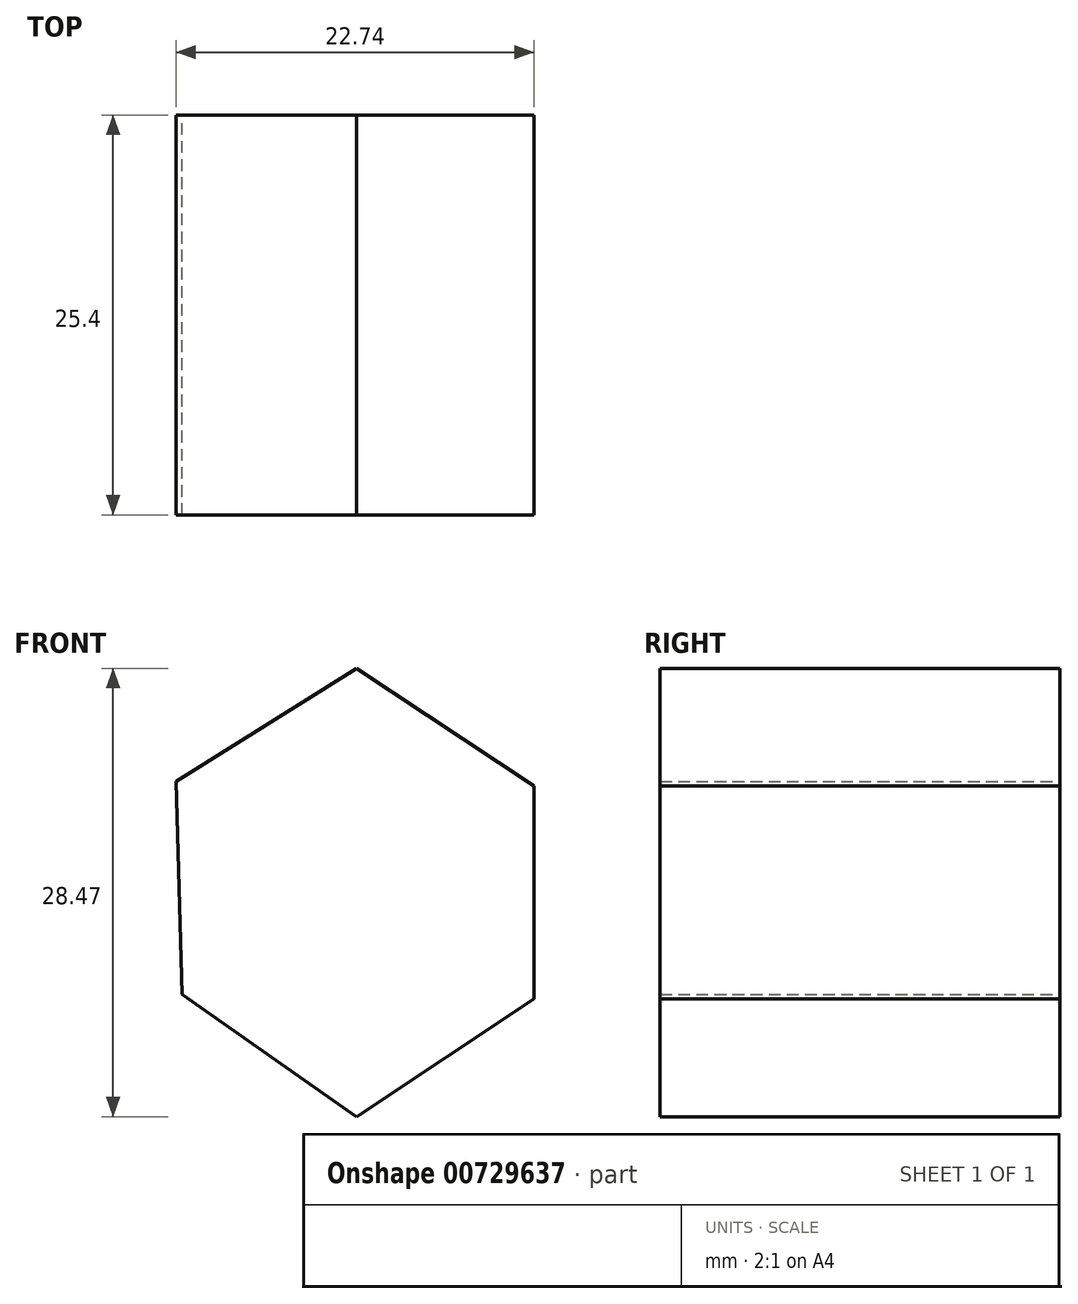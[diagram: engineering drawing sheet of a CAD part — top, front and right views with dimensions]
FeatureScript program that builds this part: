
annotation { "Feature Type Name" : "Feature", "Feature Type Description" : "" }
export const myFeature = defineFeature(function(context is Context, id is Id, definition is map)
    precondition{}
    {
        {
            var Q0;
            Q0=qCreatedBy(makeId("Front.planeOp"),FACE);
            var sketch = newSketch(context, id + "F0", { "sketchPlane" : qUnion([Q0])});
            skLineSegment(sketch, "E0", {"start": v(-53.1, 41.59) * mm, "end": v(-41.64, 48.77) * mm});
            skLineSegment(sketch, "E1", {"start": v(-41.64, 48.77) * mm, "end": v(-30.36, 41.3) * mm});
            skLineSegment(sketch, "E2", {"start": v(-30.36, 41.3) * mm, "end": v(-30.36, 27.77) * mm});
            skLineSegment(sketch, "E3", {"start": v(-30.36, 27.77) * mm, "end": v(-41.64, 20.3) * mm});
            skLineSegment(sketch, "E4", {"start": v(-41.64, 20.3) * mm, "end": v(-52.71, 28.07) * mm});
            skLineSegment(sketch, "E5", {"start": v(-52.71, 28.07) * mm, "end": v(-53.1, 41.59) * mm});
            skSolve(sketch);
        }
        {
            var Q0;
            Q0=makeQuery(id+"F0.imprint","IMPRINT",FACE,{"disambiguationData":[TD([[makeQuery(id+"F0.imprint","IMPRINT",EDGE,{"derivedFrom":sQuery(id+"F0.wireOp",EDGE,"E0")}),-1.0]])]});
            extrude(context, id + "F1", {"entities" : qUnion([Q0]), "depth" : 25.4 * mm, "offsetDistance" : 25.4 * mm});
        }
    });
